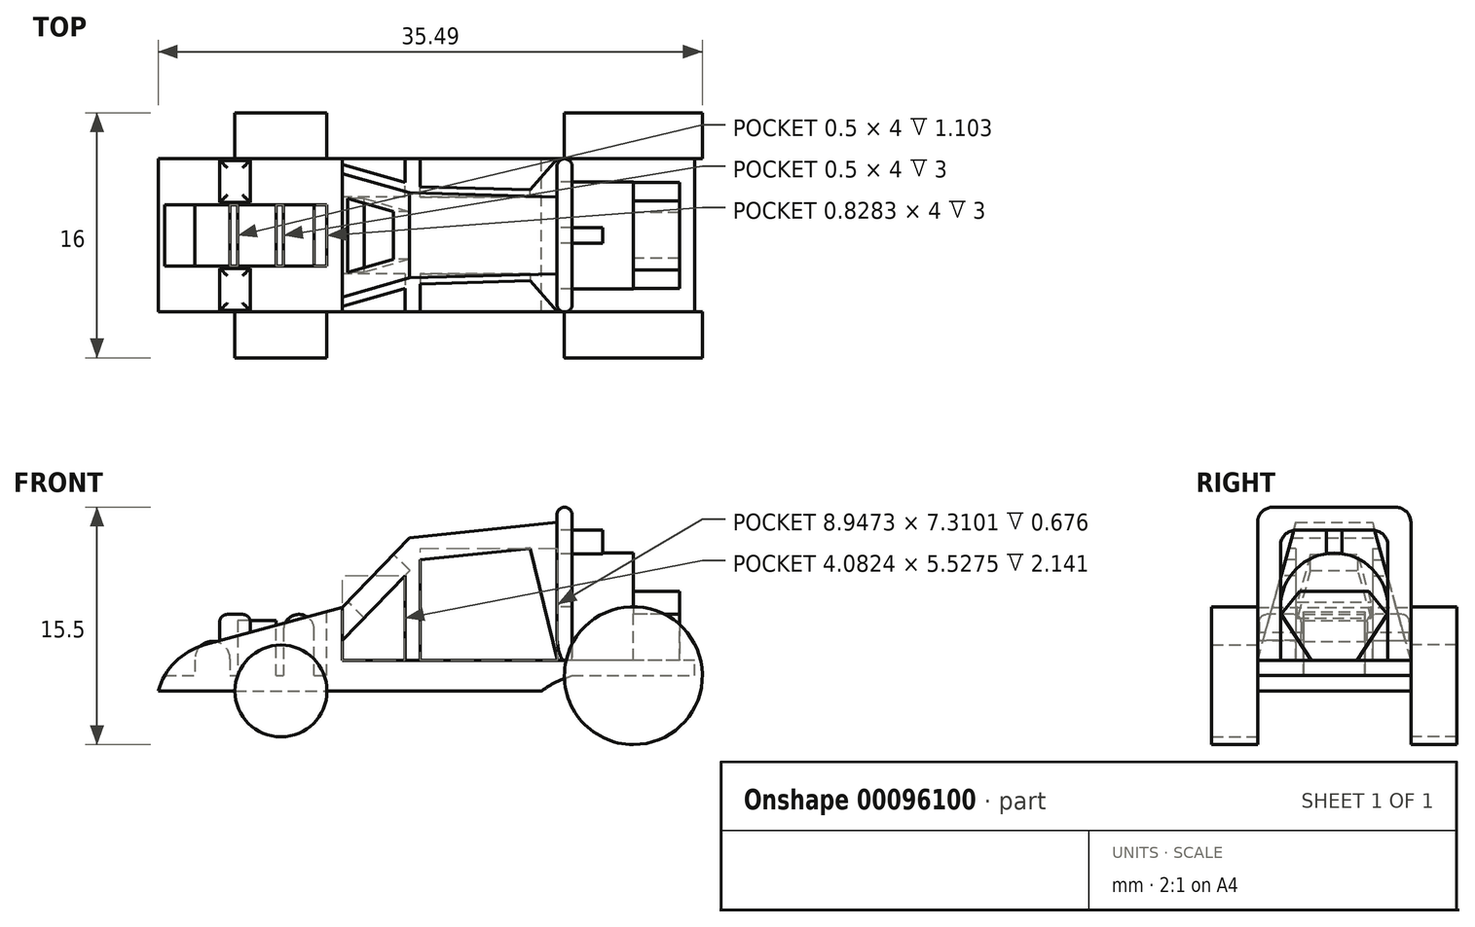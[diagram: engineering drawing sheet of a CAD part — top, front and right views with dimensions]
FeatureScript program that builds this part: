
annotation { "Feature Type Name" : "Feature", "Feature Type Description" : "" }
export const myFeature = defineFeature(function(context is Context, id is Id, definition is map)
    precondition{}
    {
        {
            var Q0;
            Q0=qCreatedBy(makeId("Front.planeOp"),FACE);
            var sketch = newSketch(context, id + "F0", { "sketchPlane" : qUnion([Q0])});
            skLineSegment(sketch, "E0", {"start": v(-25, 0) * mm, "end": v(0, 0) * mm});
            skLineSegment(sketch, "E1", {"start": v(1.98, 1) * mm, "end": v(10, 1) * mm});
            skFitSpline(sketch, "E2", {"points": [v(0, 0) * mm, v(0.84, 0.53) * mm, v(1.98, 1) * mm], "startDerivative": vector(1.69, 1.18) * mm, "endDerivative": vector(2.27, 0.83) * mm});
            skPoint(sketch, "E3.orphan", {"position": v(0, 1) * mm});
            skLineSegment(sketch, "E4", {"start": v(-13, 5.45) * mm, "end": v(-22, 3) * mm});
            skArc(sketch, "E5", {"start": v(-22, 3) * mm, "mid": v(-23.9, 1.9) * mm, "end": v(-25, 0) * mm});
            skLineSegment(sketch, "E6", {"start": v(-13, 5.45) * mm, "end": v(-8.62, 10) * mm});
            skLineSegment(sketch, "E7", {"start": v(1, 11) * mm, "end": v(1, 2) * mm});
            skLineSegment(sketch, "E8", {"start": v(-8.62, 10) * mm, "end": v(1, 11) * mm});
            skLineSegment(sketch, "E9", {"start": v(10, 1) * mm, "end": v(10, 2) * mm});
            skLineSegment(sketch, "E10", {"start": v(10, 2) * mm, "end": v(1, 2) * mm});
            skPoint(sketch, "E11.orphan", {"position": v(-11, 6) * mm});
            skSolve(sketch);
        }
        {
            var Q0;
            Q0 = qSketchRegion(id + "F0", true);
            extrude(context, id + "F1", {"entities" : qUnion([Q0]), "endBound" : BoundingType.SYMMETRIC, "depth" : 10 * mm});
        }
        {
            var Q0;
            Q0=makeQuery(id+"F1.opExtrude","SWEPT_FACE",FACE,{"disambiguationData":[OSD([sQuery(id+"F0.wireOp",EDGE,"E7")])]});
            var sketch = newSketch(context, id + "F2", { "sketchPlane" : qUnion([Q0])});
            skLineSegment(sketch, "E12", {"start": v(-3.5, 2) * mm, "end": v(-3.5, 5.5) * mm});
            skLineSegment(sketch, "E13", {"start": v(3.5, 5.5) * mm, "end": v(3.5, 2) * mm});
            skLineSegment(sketch, "E14", {"start": v(3.5, 2) * mm, "end": v(-3.5, 2) * mm});
            skArc(sketch, "E15", {"start": v(3.5, 5.5) * mm, "mid": v(0, 9) * mm, "end": v(-3.5, 5.5) * mm});
            skSolve(sketch);
        }
        {
            var Q0;
            Q0 = qSketchRegion(id + "F2", true);
            extrude(context, id + "F3", {"entities" : qUnion([Q0]), "operationType" : NewBodyOperationType.ADD, "depth" : 5 * mm});
        }
        {
            var Q0;
            Q0=makeQuery(id+"F1.opExtrude","SWEPT_FACE",FACE,{"disambiguationData":[OSD([sQuery(id+"F0.wireOp",EDGE,"E7")])]});
            var sketch = newSketch(context, id + "F4", { "sketchPlane" : qUnion([Q0])});
            skLineSegment(sketch, "E16", {"start": v(-0.5, 8.96) * mm, "end": v(-0.5, 10.5) * mm});
            skLineSegment(sketch, "E17", {"start": v(-0.5, 10.5) * mm, "end": v(0.5, 10.5) * mm});
            skLineSegment(sketch, "E18", {"start": v(0.5, 10.5) * mm, "end": v(0.5, 8.96) * mm});
            skLineSegment(sketch, "E19", {"start": v(-0.5, 8.96) * mm, "end": v(0.5, 8.96) * mm});
            skSolve(sketch);
        }
        {
            var Q0;
            Q0 = qSketchRegion(id + "F4", true);
            extrude(context, id + "F5", {"entities" : qUnion([Q0]), "depth" : 3 * mm});
        }
        {
            var Q0;
            Q0=makeQuery(id+"F1.opExtrude","SWEPT_FACE",FACE,{"disambiguationData":[OSD([sQuery(id+"F0.wireOp",EDGE,"E7")])]});
            var sketch = newSketch(context, id + "F6", { "sketchPlane" : qUnion([Q0])});
            skLineSegment(sketch, "E20", {"start": v(-5, 2) * mm, "end": v(-2.5, 11) * mm});
            skLineSegment(sketch, "E21", {"start": v(-6.27, 11) * mm, "end": v(-5, 2) * mm});
            skLineSegment(sketch, "E22", {"start": v(-2.5, 11) * mm, "end": v(2.5, 11) * mm});
            skLineSegment(sketch, "E23", {"start": v(2.5, 11) * mm, "end": v(5, 2) * mm});
            skLineSegment(sketch, "E24", {"start": v(5, 2) * mm, "end": v(5.85, 13.35) * mm});
            skLineSegment(sketch, "E25", {"start": v(5.85, 13.35) * mm, "end": v(-6.93, 13.35) * mm});
            skLineSegment(sketch, "E26", {"start": v(-6.93, 13.35) * mm, "end": v(-6.27, 11) * mm});
            skSolve(sketch);
        }
        {
            var Q0;
            Q0 = qSketchRegion(id + "F6", true);
            extrude(context, id + "F7", {"entities" : qUnion([Q0]), "operationType" : NewBodyOperationType.REMOVE, "oppositeDirection" : true, "depth" : 14 * mm});
        }
        {
            var Q0;
            Q0=makeQuery(id+"F3.opExtrude","CAP_FACE",FACE,{"disambiguationData":[OSD([sQuery(id+"F2.wireOp",EDGE,"E12"),sQuery(id+"F2.wireOp",EDGE,"E13"),sQuery(id+"F2.wireOp",EDGE,"E14"),sQuery(id+"F2.wireOp",EDGE,"E15")])],"isStart":false});
            var sketch = newSketch(context, id + "F8", { "sketchPlane" : qUnion([Q0])});
            skLineSegment(sketch, "E27", {"start": v(-3.46, 5) * mm, "end": v(-1.5, 2) * mm});
            skLineSegment(sketch, "E28", {"start": v(-1.5, 2) * mm, "end": v(1.5, 2) * mm});
            skLineSegment(sketch, "E29", {"start": v(1.5, 2) * mm, "end": v(3.46, 5) * mm});
            skLineSegment(sketch, "E30", {"start": v(3.46, 5) * mm, "end": v(2.25, 6.5) * mm});
            skLineSegment(sketch, "E31", {"start": v(2.25, 6.5) * mm, "end": v(-2.25, 6.5) * mm});
            skLineSegment(sketch, "E32", {"start": v(-2.25, 6.5) * mm, "end": v(-3.46, 5) * mm});
            skSolve(sketch);
        }
        {
            var Q0;
            Q0 = qSketchRegion(id + "F8", true);
            extrude(context, id + "F9", {"entities" : qUnion([Q0]), "operationType" : NewBodyOperationType.ADD, "depth" : 3 * mm});
        }
        {
            var Q0;
            Q0=makeQuery(id+"F1.opExtrude","SWEPT_FACE",FACE,{"disambiguationData":[OSD([sQuery(id+"F0.wireOp",EDGE,"E7")])]});
            var sketch = newSketch(context, id + "F10", { "sketchPlane" : qUnion([Q0])});
            skLineSegment(sketch, "E33", {"start": v(-5, 2) * mm, "end": v(-5, 11) * mm});
            skLineSegment(sketch, "E34", {"start": v(-4, 12) * mm, "end": v(4, 12) * mm});
            skLineSegment(sketch, "E35", {"start": v(5, 11) * mm, "end": v(5, 2) * mm});
            skPoint(sketch, "E36.endSnap0", {"position": v(4.25, 2) * mm});
            skPoint(sketch, "E37.visualSharp", {"position": v(-5, 12) * mm});
            skArc(sketch, "E37.filletArc", {"start": v(-4, 12) * mm, "mid": v(-4.7, 11.7) * mm, "end": v(-5, 11) * mm});
            skPoint(sketch, "E38.visualSharp", {"position": v(5, 12) * mm});
            skArc(sketch, "E38.filletArc", {"start": v(5, 11) * mm, "mid": v(4.7, 11.7) * mm, "end": v(4, 12) * mm});
            skLineSegment(sketch, "E39", {"start": v(-3.5, 9.5) * mm, "end": v(-3.5, 2) * mm});
            skLineSegment(sketch, "E40", {"start": v(-2.5, 10.5) * mm, "end": v(2.5, 10.5) * mm});
            skLineSegment(sketch, "E41", {"start": v(3.5, 9.5) * mm, "end": v(3.5, 2) * mm});
            skArc(sketch, "E42.filletArc", {"start": v(-2.5, 10.5) * mm, "mid": v(-3.2, 10.2) * mm, "end": v(-3.5, 9.5) * mm});
            skArc(sketch, "E43.filletArc", {"start": v(3.5, 9.5) * mm, "mid": v(3.2, 10.2) * mm, "end": v(2.5, 10.5) * mm});
            skLineSegment(sketch, "E44", {"start": v(-5, 2) * mm, "end": v(-3.5, 2) * mm});
            skLineSegment(sketch, "E45", {"start": v(3.5, 2) * mm, "end": v(5, 2) * mm});
            skSolve(sketch);
        }
        {
            var Q0;
            Q0 = qSketchRegion(id + "F10", true);
            extrude(context, id + "F11", {"entities" : qUnion([Q0]), "operationType" : NewBodyOperationType.ADD, "depth" : 1 * mm});
        }
        {
            var Q0;
            Q0=makeQuery(id+"F11.opExtrude","CAP_EDGE",EDGE,{"disambiguationData":[OSD([sQuery(id+"F10.wireOp",EDGE,"E33")])],"isStart":false});
            var Q1;
            Q1=makeQuery(id+"F11.opExtrude","CAP_EDGE",EDGE,{"disambiguationData":[OSD([sQuery(id+"F10.wireOp",EDGE,"E33")])],"isStart":true});
            fillet(context, id + "F12", {"entities" : qUnion([Q0, Q1]), "radius" : 0.5 * mm, "tangentPropagation" : true, "allowEdgeOverflow" : false});
        }
        {
            var Q0;
            Q0=makeQuery(id+"F11.boolean.opBoolean","MERGE",FACE,{"derivedFrom":[makeQuery(id+"F1.opExtrude","CAP_FACE",FACE,{"disambiguationData":[OSD([sQuery(id+"F0.wireOp",EDGE,"E0"),sQuery(id+"F0.wireOp",EDGE,"E1"),sQuery(id+"F0.wireOp",EDGE,"E2"),sQuery(id+"F0.wireOp",EDGE,"E4"),sQuery(id+"F0.wireOp",EDGE,"E5"),sQuery(id+"F0.wireOp",EDGE,"E6"),sQuery(id+"F0.wireOp",EDGE,"E7"),sQuery(id+"F0.wireOp",EDGE,"E8"),sQuery(id+"F0.wireOp",EDGE,"E9"),sQuery(id+"F0.wireOp",EDGE,"E10")])],"isStart":false}),makeQuery(id+"F11.opExtrude","SWEPT_FACE",FACE,{"disambiguationData":[OSD([sQuery(id+"F10.wireOp",EDGE,"E33")])]})]});
            var sketch = newSketch(context, id + "F13", { "sketchPlane" : qUnion([Q0])});
            skLineSegment(sketch, "E46.0", {"start": v(-8.92, 7.53) * mm, "end": v(-13, 3.3) * mm});
            skLineSegment(sketch, "E46.1", {"start": v(-0.75, 9.31) * mm, "end": v(-7.92, 8.56) * mm});
            skLineSegment(sketch, "E47", {"start": v(-0.75, 9.31) * mm, "end": v(1.03, 2) * mm});
            skLineSegment(sketch, "E48", {"start": v(-7.92, 8.56) * mm, "end": v(-7.92, 2) * mm});
            skLineSegment(sketch, "E49", {"start": v(-7.92, 2) * mm, "end": v(1.03, 2) * mm});
            skLineSegment(sketch, "E50", {"start": v(-8.92, 7.53) * mm, "end": v(-8.92, 2) * mm});
            skLineSegment(sketch, "E51", {"start": v(-8.92, 2) * mm, "end": v(-13, 2) * mm});
            skLineSegment(sketch, "E52", {"start": v(-13, 2) * mm, "end": v(-13, 3.3) * mm});
            skSolve(sketch);
        }
        {
            var Q0;
            Q0 = qSketchRegion(id + "F13", true);
            extrude(context, id + "F14", {"entities" : qUnion([Q0]), "operationType" : NewBodyOperationType.REMOVE, "oppositeDirection" : true, "depth" : 2.5 * mm});
        }
        {
            var Q0;
            Q0=makeQuery(id+"F11.boolean.opBoolean","MERGE",FACE,{"derivedFrom":[makeQuery(id+"F1.opExtrude","CAP_FACE",FACE,{"disambiguationData":[OSD([sQuery(id+"F0.wireOp",EDGE,"E0"),sQuery(id+"F0.wireOp",EDGE,"E1"),sQuery(id+"F0.wireOp",EDGE,"E2"),sQuery(id+"F0.wireOp",EDGE,"E4"),sQuery(id+"F0.wireOp",EDGE,"E5"),sQuery(id+"F0.wireOp",EDGE,"E6"),sQuery(id+"F0.wireOp",EDGE,"E7"),sQuery(id+"F0.wireOp",EDGE,"E8"),sQuery(id+"F0.wireOp",EDGE,"E9"),sQuery(id+"F0.wireOp",EDGE,"E10")])],"isStart":true}),makeQuery(id+"F11.opExtrude","SWEPT_FACE",FACE,{"disambiguationData":[OSD([sQuery(id+"F10.wireOp",EDGE,"E35")])]})]});
            var sketch = newSketch(context, id + "F15", { "sketchPlane" : qUnion([Q0])});
            skLineSegment(sketch, "E53.0", {"start": v(0.75, 9.31) * mm, "end": v(-1.03, 2) * mm});
            skLineSegment(sketch, "E54.0", {"start": v(0.75, 9.31) * mm, "end": v(7.92, 8.56) * mm});
            skLineSegment(sketch, "E55.0", {"start": v(7.92, 8.56) * mm, "end": v(7.92, 2) * mm});
            skLineSegment(sketch, "E56.0", {"start": v(13, 2) * mm, "end": v(8.92, 2) * mm});
            skLineSegment(sketch, "E57.0", {"start": v(8.92, 7.53) * mm, "end": v(8.92, 2) * mm});
            skLineSegment(sketch, "E58.0", {"start": v(8.92, 7.53) * mm, "end": v(13, 3.3) * mm});
            skLineSegment(sketch, "E59.0", {"start": v(13, 2) * mm, "end": v(13, 3.3) * mm});
            skPoint(sketch, "E60.orphan", {"position": v(13, 5.45) * mm});
            skLineSegment(sketch, "E61.trimOffspring", {"start": v(7.92, 2) * mm, "end": v(-1.03, 2) * mm});
            skPoint(sketch, "E62.orphan", {"position": v(-1.5, 2) * mm});
            skSolve(sketch);
        }
        {
            var Q0;
            Q0 = qSketchRegion(id + "F15", true);
            extrude(context, id + "F16", {"entities" : qUnion([Q0]), "operationType" : NewBodyOperationType.REMOVE, "oppositeDirection" : true, "depth" : 2.5 * mm});
        }
        {
            var Q0;
            Q0=qCreatedBy(makeId("Top.planeOp"),FACE);
            cPlane(context, id + "F17", {"entities" : qUnion([Q0]), "cplaneType" : CPlaneType.OFFSET, "offset" : 10 * mm, "width" : 150 * mm, "height" : 150 * mm});
        }
        {
            var Q0;
            Q0=qCreatedBy(id+"F17.planeOp",FACE);
            var sketch = newSketch(context, id + "F18", { "sketchPlane" : qUnion([Q0])});
            skLineSegment(sketch, "E63.bottom", {"start": v(-26, 2) * mm, "end": v(-14, 2) * mm});
            skLineSegment(sketch, "E63.top", {"start": v(-26, -2) * mm, "end": v(-14, -2) * mm});
            skLineSegment(sketch, "E63.left", {"start": v(-26, 2) * mm, "end": v(-26, -2) * mm});
            skLineSegment(sketch, "E63.right", {"start": v(-14, 2) * mm, "end": v(-14, -2) * mm});
            skSolve(sketch);
        }
        {
            var Q0;
            Q0 = qSketchRegion(id + "F18", true);
            extrude(context, id + "F19", {"entities" : qUnion([Q0]), "operationType" : NewBodyOperationType.REMOVE, "oppositeDirection" : true, "depth" : 9 * mm});
        }
        {
            var Q0;
            Q0=qCreatedBy(makeId("Front.planeOp"),FACE);
            var sketch = newSketch(context, id + "F20", { "sketchPlane" : qUnion([Q0])});
            skLineSegment(sketch, "E64.0", {"start": v(-22.6, 1) * mm, "end": v(-20.33, 1) * mm});
            skLineSegment(sketch, "E65", {"start": v(-14.83, 1) * mm, "end": v(-14.83, 4) * mm});
            skLineSegment(sketch, "E66", {"start": v(-16.83, 4) * mm, "end": v(-16.83, 1) * mm});
            skArc(sketch, "E67", {"start": v(-14.83, 4) * mm, "mid": v(-15.83, 5) * mm, "end": v(-16.83, 4) * mm});
            skLineSegment(sketch, "E68", {"start": v(-17.33, 1) * mm, "end": v(-17.33, 4.6) * mm});
            skLineSegment(sketch, "E69", {"start": v(-17.33, 4.6) * mm, "end": v(-19.83, 4.6) * mm});
            skLineSegment(sketch, "E70", {"start": v(-19.83, 4.6) * mm, "end": v(-19.83, 1) * mm});
            skArc(sketch, "E71", {"start": v(-20.33, 2.1) * mm, "mid": v(-21.5, 3.24) * mm, "end": v(-22.6, 2.03) * mm});
            skLineSegment(sketch, "E72", {"start": v(-20.33, 2.1) * mm, "end": v(-20.33, 1) * mm});
            skLineSegment(sketch, "E73", {"start": v(-22.6, 2.03) * mm, "end": v(-22.6, 1) * mm});
            skPoint(sketch, "E74.orphan", {"position": v(-24.59, 1) * mm});
            skLineSegment(sketch, "E75.trimOffspring", {"start": v(-19.83, 1) * mm, "end": v(-17.33, 1) * mm});
            skLineSegment(sketch, "E76.trimOffspring", {"start": v(-16.83, 1) * mm, "end": v(-14.83, 1) * mm});
            skPoint(sketch, "E77.orphan", {"position": v(-14, 1) * mm});
            skSolve(sketch);
        }
        {
            var Q0;
            Q0 = qSketchRegion(id + "F20", true);
            extrude(context, id + "F21", {"entities" : qUnion([Q0]), "operationType" : NewBodyOperationType.ADD, "endBound" : BoundingType.SYMMETRIC, "depth" : 4 * mm});
        }
        {
            var Q0;
            Q0=makeQuery(id+"F11.boolean.opBoolean","MERGE",FACE,{"derivedFrom":[makeQuery(id+"F1.opExtrude","CAP_FACE",FACE,{"disambiguationData":[OSD([sQuery(id+"F0.wireOp",EDGE,"E0"),sQuery(id+"F0.wireOp",EDGE,"E1"),sQuery(id+"F0.wireOp",EDGE,"E2"),sQuery(id+"F0.wireOp",EDGE,"E4"),sQuery(id+"F0.wireOp",EDGE,"E5"),sQuery(id+"F0.wireOp",EDGE,"E6"),sQuery(id+"F0.wireOp",EDGE,"E7"),sQuery(id+"F0.wireOp",EDGE,"E8"),sQuery(id+"F0.wireOp",EDGE,"E9"),sQuery(id+"F0.wireOp",EDGE,"E10")])],"isStart":false}),makeQuery(id+"F11.opExtrude","SWEPT_FACE",FACE,{"disambiguationData":[OSD([sQuery(id+"F10.wireOp",EDGE,"E33")])]})]});
            var sketch = newSketch(context, id + "F22", { "sketchPlane" : qUnion([Q0])});
            skCircle(sketch, "E78", {"center": v(-17, 0) * mm, "radius": 3 * mm});
            skCircle(sketch, "E79", {"center": v(6, 1) * mm, "radius": 4.5 * mm});
            skLineSegment(sketch, "E80", {"start": v(-17.06, -3) * mm, "end": v(10.56, -3.55) * mm});
            skSolve(sketch);
        }
        {
            var Q0;
            Q0 = qSketchRegion(id + "F22", true);
            extrude(context, id + "F23", {"entities" : qUnion([Q0]), "operationType" : NewBodyOperationType.ADD, "depth" : 3 * mm});
        }
        {
            var Q0;
            Q0=makeQuery(id+"F11.boolean.opBoolean","MERGE",FACE,{"derivedFrom":[makeQuery(id+"F1.opExtrude","CAP_FACE",FACE,{"disambiguationData":[OSD([sQuery(id+"F0.wireOp",EDGE,"E0"),sQuery(id+"F0.wireOp",EDGE,"E1"),sQuery(id+"F0.wireOp",EDGE,"E2"),sQuery(id+"F0.wireOp",EDGE,"E4"),sQuery(id+"F0.wireOp",EDGE,"E5"),sQuery(id+"F0.wireOp",EDGE,"E6"),sQuery(id+"F0.wireOp",EDGE,"E7"),sQuery(id+"F0.wireOp",EDGE,"E8"),sQuery(id+"F0.wireOp",EDGE,"E9"),sQuery(id+"F0.wireOp",EDGE,"E10")])],"isStart":true}),makeQuery(id+"F11.opExtrude","SWEPT_FACE",FACE,{"disambiguationData":[OSD([sQuery(id+"F10.wireOp",EDGE,"E35")])]})]});
            var sketch = newSketch(context, id + "F24", { "sketchPlane" : qUnion([Q0])});
            skArc(sketch, "E81.0", {"start": v(-1.5, 0.82) * mm, "mid": v(-10.47, 0.59) * mm, "end": v(-1.6, 2) * mm});
            skArc(sketch, "E82.0", {"start": v(14, 0) * mm, "mid": v(17, 3) * mm, "end": v(20, 0) * mm});
            skArc(sketch, "E83.0", {"start": v(20, 0) * mm, "mid": v(17, -3) * mm, "end": v(14, 0) * mm});
            skArc(sketch, "E84.0", {"start": v(-1.6, 2) * mm, "mid": v(-1.5, 1.41) * mm, "end": v(-1.5, 0.82) * mm});
            skSolve(sketch);
        }
        {
            var Q0;
            Q0 = qSketchRegion(id + "F24", true);
            extrude(context, id + "F25", {"entities" : qUnion([Q0]), "operationType" : NewBodyOperationType.ADD, "depth" : 3 * mm});
        }
        {
            var Q0;
            Q0=qCreatedBy(makeId("Top.planeOp"),FACE);
            var sketch = newSketch(context, id + "F26", { "sketchPlane" : qUnion([Q0])});
            skLineSegment(sketch, "E85.bottom", {"start": v(-21, 4.9) * mm, "end": v(-19, 4.9) * mm});
            skLineSegment(sketch, "E85.top", {"start": v(-21, 2.15) * mm, "end": v(-19, 2.15) * mm});
            skLineSegment(sketch, "E85.left", {"start": v(-21, 4.9) * mm, "end": v(-21, 2.15) * mm});
            skLineSegment(sketch, "E85.right", {"start": v(-19, 4.9) * mm, "end": v(-19, 2.15) * mm});
            skLineSegment(sketch, "E86.bottom", {"start": v(-21, -2.15) * mm, "end": v(-19, -2.15) * mm});
            skLineSegment(sketch, "E86.top", {"start": v(-21, -4.9) * mm, "end": v(-19, -4.9) * mm});
            skLineSegment(sketch, "E86.left", {"start": v(-21, -2.15) * mm, "end": v(-21, -4.9) * mm});
            skLineSegment(sketch, "E86.right", {"start": v(-19, -2.15) * mm, "end": v(-19, -4.9) * mm});
            skSolve(sketch);
        }
        {
            var Q0;
            Q0 = qSketchRegion(id + "F26", true);
            extrude(context, id + "F27", {"entities" : qUnion([Q0]), "operationType" : NewBodyOperationType.ADD, "depth" : 5 * mm});
        }
        {
            var Q0;
            Q0=makeQuery(id+"F27.opExtrude","CAP_EDGE",EDGE,{"disambiguationData":[OSD([sQuery(id+"F26.wireOp",EDGE,"E85.left")])],"isStart":false});
            var Q1;
            Q1=makeQuery(id+"F27.opExtrude","CAP_EDGE",EDGE,{"disambiguationData":[OSD([sQuery(id+"F26.wireOp",EDGE,"E85.right")])],"isStart":false});
            var Q2;
            Q2=makeQuery(id+"F27.opExtrude","CAP_EDGE",EDGE,{"disambiguationData":[OSD([sQuery(id+"F26.wireOp",EDGE,"E85.bottom")])],"isStart":false});
            var Q3;
            Q3=makeQuery(id+"F27.opExtrude","CAP_EDGE",EDGE,{"disambiguationData":[OSD([sQuery(id+"F26.wireOp",EDGE,"E85.top")])],"isStart":false});
            var Q4;
            Q4=makeQuery(id+"F27.opExtrude","CAP_EDGE",EDGE,{"disambiguationData":[OSD([sQuery(id+"F26.wireOp",EDGE,"E86.top")])],"isStart":false});
            var Q5;
            Q5=makeQuery(id+"F27.opExtrude","CAP_EDGE",EDGE,{"disambiguationData":[OSD([sQuery(id+"F26.wireOp",EDGE,"E86.left")])],"isStart":false});
            var Q6;
            Q6=makeQuery(id+"F27.opExtrude","CAP_EDGE",EDGE,{"disambiguationData":[OSD([sQuery(id+"F26.wireOp",EDGE,"E86.bottom")])],"isStart":false});
            var Q7;
            Q7=makeQuery(id+"F27.opExtrude","CAP_EDGE",EDGE,{"disambiguationData":[OSD([sQuery(id+"F26.wireOp",EDGE,"E86.right")])],"isStart":false});
            fillet(context, id + "F28", {"entities" : qUnion([Q0, Q1, Q2, Q3, Q4, Q5, Q6, Q7]), "radius" : 0.5 * mm, "tangentPropagation" : true, "allowEdgeOverflow" : false});
        }
        {
            var Q0;
            Q0=makeQuery(id+"F1.opExtrude","SWEPT_FACE",FACE,{"disambiguationData":[OSD([sQuery(id+"F0.wireOp",EDGE,"E6")])]});
            var sketch = newSketch(context, id + "F29", { "sketchPlane" : qUnion([Q0])});
            skLineSegment(sketch, "E87.0", {"start": v(1.55, -0.28) * mm, "end": v(-1.55, -0.28) * mm});
            skLineSegment(sketch, "E88.0", {"start": v(-2.41, -4.6) * mm, "end": v(-1.55, -0.28) * mm});
            skLineSegment(sketch, "E89.0", {"start": v(1.55, -0.28) * mm, "end": v(2.41, -4.6) * mm});
            skLineSegment(sketch, "E90.0", {"start": v(2.41, -4.6) * mm, "end": v(-2.41, -4.6) * mm});
            skSolve(sketch);
        }
        {
            var Q0;
            Q0 = qSketchRegion(id + "F29", true);
            extrude(context, id + "F30", {"entities" : qUnion([Q0]), "operationType" : NewBodyOperationType.REMOVE, "oppositeDirection" : true, "depth" : 1.5 * mm});
        }
    });
